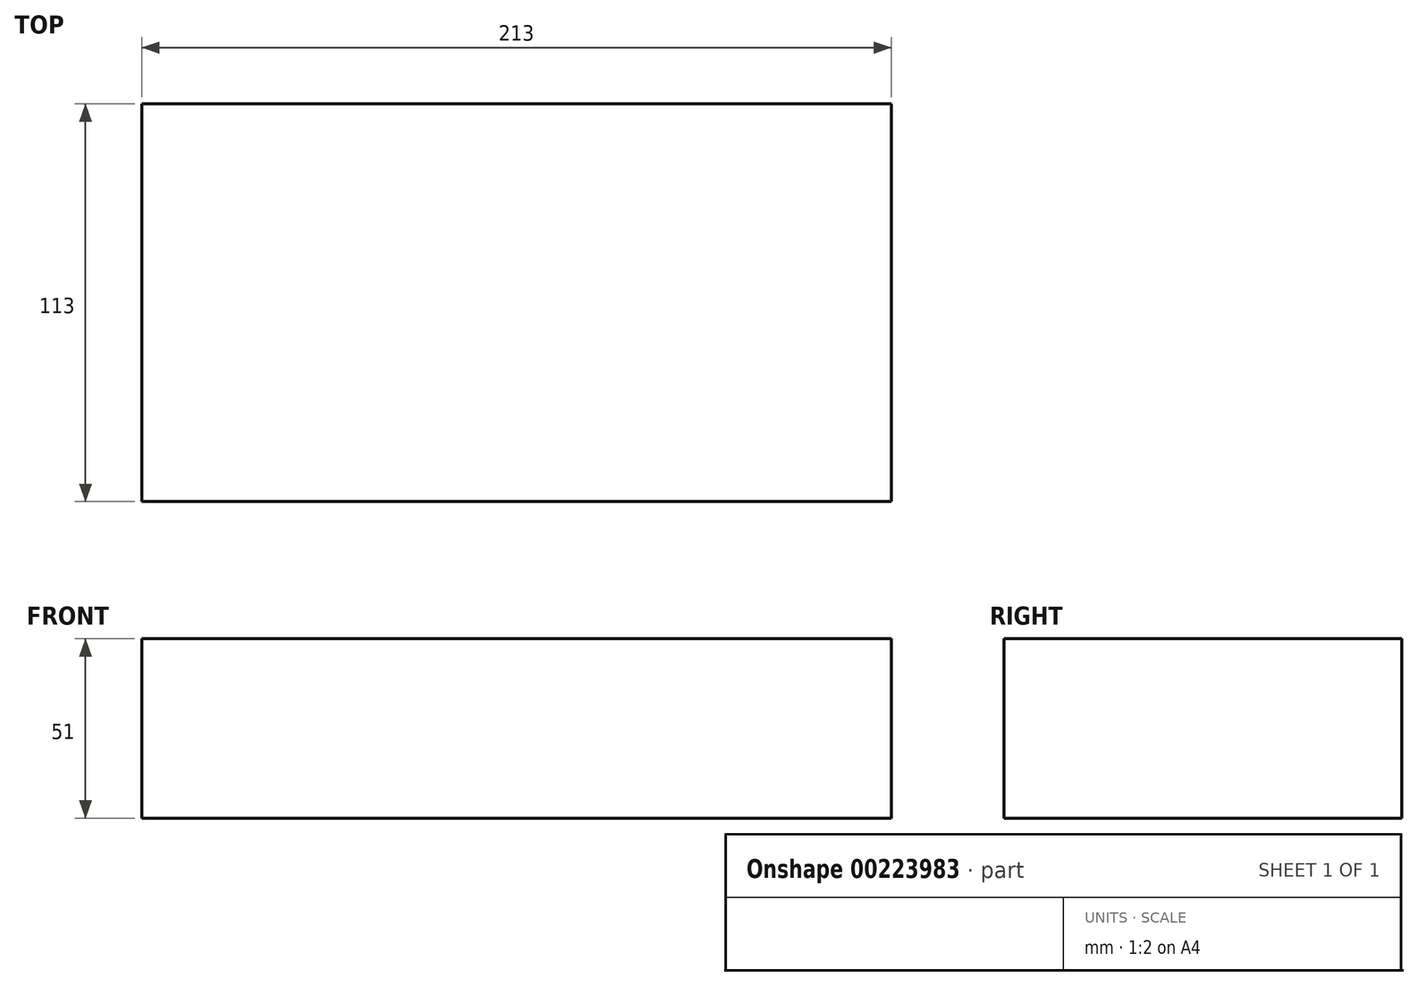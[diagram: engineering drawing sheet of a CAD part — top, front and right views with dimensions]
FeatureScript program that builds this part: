
annotation { "Feature Type Name" : "Feature", "Feature Type Description" : "" }
export const myFeature = defineFeature(function(context is Context, id is Id, definition is map)
    precondition{}
    {
        {
            var Q0;
            Q0=qCreatedBy(makeId("Top.planeOp"),FACE);
            var sketch = newSketch(context, id + "F0", { "sketchPlane" : qUnion([Q0])});
            skLineSegment(sketch, "E0.bottom", {"start": v(106.5, -56.5) * mm, "end": v(-106.5, -56.5) * mm});
            skLineSegment(sketch, "E0.top", {"start": v(106.5, 56.5) * mm, "end": v(-106.5, 56.5) * mm});
            skLineSegment(sketch, "E0.left", {"start": v(106.5, -56.5) * mm, "end": v(106.5, 56.5) * mm});
            skLineSegment(sketch, "E0.right", {"start": v(-106.5, -56.5) * mm, "end": v(-106.5, 56.5) * mm});
            skPoint(sketch, "E0.middle", {"position": v(0, 0) * mm});
            skSolve(sketch);
        }
        {
            var Q0;
            Q0 = qSketchRegion(id + "F0", true);
            extrude(context, id + "F1", {"entities" : qUnion([Q0]), "depth" : 51 * mm});
        }
    });
